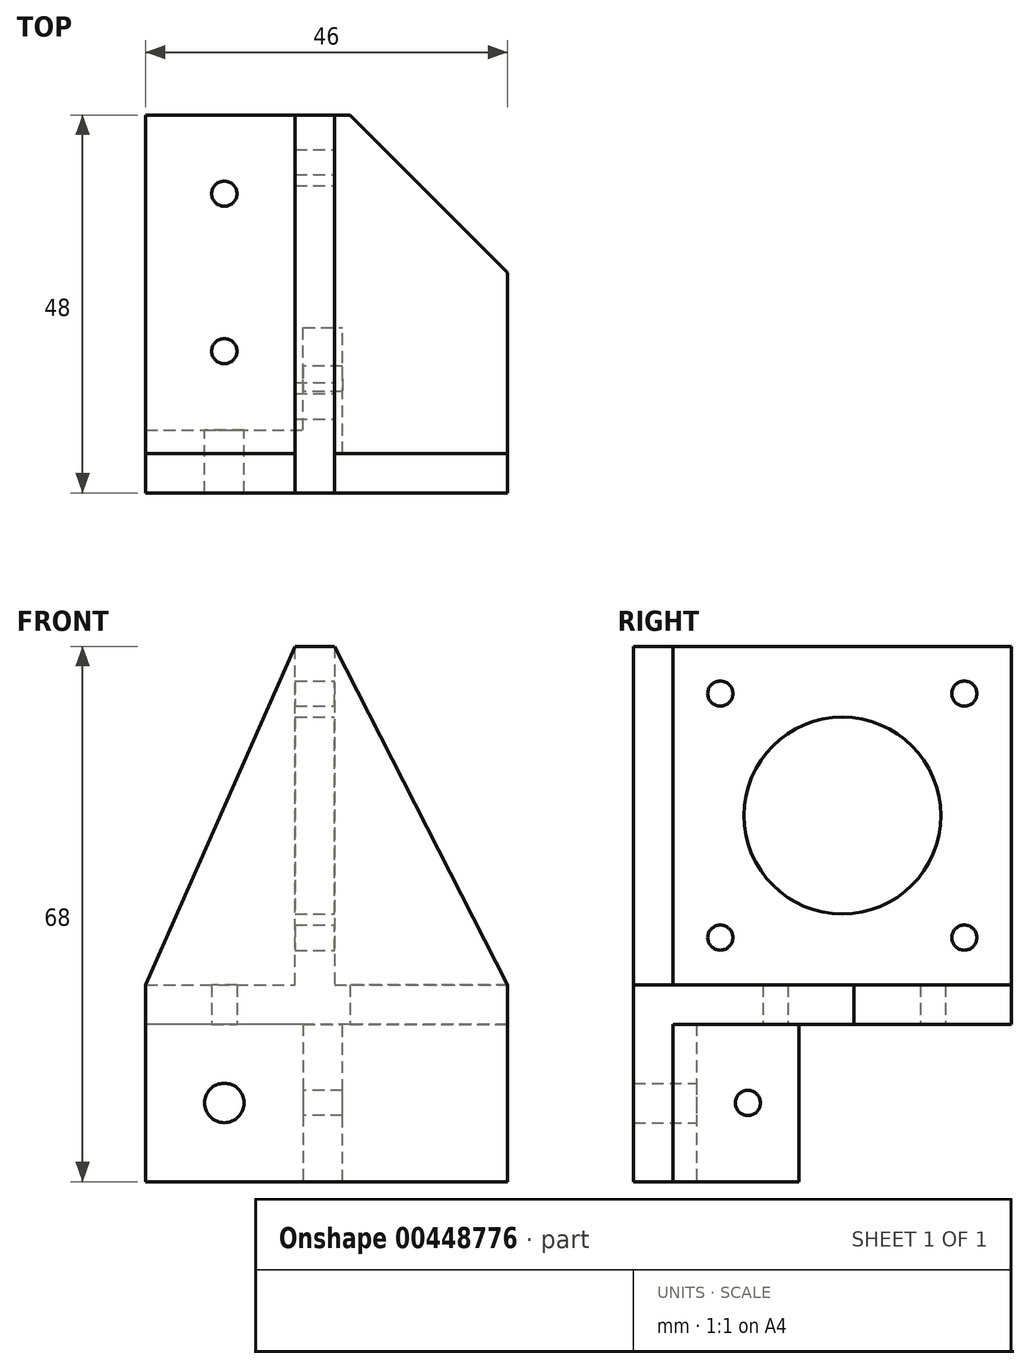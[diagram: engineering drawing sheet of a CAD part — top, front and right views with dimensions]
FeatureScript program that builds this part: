
annotation { "Feature Type Name" : "Feature", "Feature Type Description" : "" }
export const myFeature = defineFeature(function(context is Context, id is Id, definition is map)
    precondition{}
    {
        {
            var Q0;
            Q0=qCreatedBy(makeId("Front.planeOp"),FACE);
            var sketch = newSketch(context, id + "F0", { "sketchPlane" : qUnion([Q0])});
            skLineSegment(sketch, "E0.bottom", {"start": v(0, 20) * mm, "end": v(20, 20) * mm, "construction": true});
            skLineSegment(sketch, "E0.top", {"start": v(0, 0) * mm, "end": v(20, 0) * mm, "construction": true});
            skLineSegment(sketch, "E0.left", {"start": v(0, 20) * mm, "end": v(0, 0) * mm, "construction": true});
            skLineSegment(sketch, "E0.right", {"start": v(20, 20) * mm, "end": v(20, 0) * mm, "construction": true});
            skLineSegment(sketch, "E1", {"start": v(0, 20) * mm, "end": v(0, 25) * mm});
            skLineSegment(sketch, "E2", {"start": v(46, 25) * mm, "end": v(46, 20) * mm});
            skLineSegment(sketch, "E3", {"start": v(46, 20) * mm, "end": v(25, 20) * mm});
            skLineSegment(sketch, "E4", {"start": v(25, 20) * mm, "end": v(25, 0) * mm});
            skLineSegment(sketch, "E5", {"start": v(25, 0) * mm, "end": v(20, 0) * mm});
            skLineSegment(sketch, "E6", {"start": v(20, 20) * mm, "end": v(0, 20) * mm});
            skLineSegment(sketch, "E7", {"start": v(20, 20) * mm, "end": v(20, 0) * mm});
            skLineSegment(sketch, "E8", {"start": v(0, 25) * mm, "end": v(19, 25) * mm});
            skLineSegment(sketch, "E9", {"start": v(19, 25) * mm, "end": v(19, 68) * mm});
            skLineSegment(sketch, "E10", {"start": v(19, 68) * mm, "end": v(24, 68) * mm});
            skLineSegment(sketch, "E11", {"start": v(24, 68) * mm, "end": v(24, 25) * mm});
            skLineSegment(sketch, "E12", {"start": v(24, 25) * mm, "end": v(46, 25) * mm});
            skSolve(sketch);
        }
        {
            var Q0;
            Q0=makeQuery(id+"F0.imprint","IMPRINT",FACE,{"disambiguationData":[TD([[makeQuery(id+"F0.imprint","IMPRINT",EDGE,{"derivedFrom":sQuery(id+"F0.wireOp",EDGE,"E1")}),-1.0]])]});
            extrude(context, id + "F1", {"entities" : qUnion([Q0]), "depth" : 43 * mm});
        }
        {
            var Q0;
            Q0=makeQuery(id+"F1.opExtrude","CAP_FACE",FACE,{"disambiguationData":[OSD([sQuery(id+"F0.wireOp",EDGE,"E1"),sQuery(id+"F0.wireOp",EDGE,"E2"),sQuery(id+"F0.wireOp",EDGE,"E3"),sQuery(id+"F0.wireOp",EDGE,"E4"),sQuery(id+"F0.wireOp",EDGE,"E5"),sQuery(id+"F0.wireOp",EDGE,"E6"),sQuery(id+"F0.wireOp",EDGE,"E7"),sQuery(id+"F0.wireOp",EDGE,"E8"),sQuery(id+"F0.wireOp",EDGE,"E9"),sQuery(id+"F0.wireOp",EDGE,"E10"),sQuery(id+"F0.wireOp",EDGE,"E11"),sQuery(id+"F0.wireOp",EDGE,"E12")])],"isStart":false});
            var sketch = newSketch(context, id + "F2", { "sketchPlane" : qUnion([Q0])});
            skLineSegment(sketch, "E13.bottom", {"start": v(0, 20) * mm, "end": v(20, 20) * mm});
            skLineSegment(sketch, "E13.top", {"start": v(0, 0) * mm, "end": v(20, 0) * mm});
            skLineSegment(sketch, "E13.left", {"start": v(0, 20) * mm, "end": v(0, 0) * mm});
            skLineSegment(sketch, "E13.right", {"start": v(20, 20) * mm, "end": v(20, 0) * mm});
            skSolve(sketch);
        }
        {
            var Q0;
            Q0=qSketchRegion(id+"F2",true);
            extrude(context, id + "F3", {"entities" : qUnion([Q0]), "operationType" : NewBodyOperationType.ADD, "oppositeDirection" : true, "depth" : 3 * mm});
        }
        {
            var Q0;
            Q0=makeQuery(id+"F1.opExtrude","SWEPT_FACE",FACE,{"disambiguationData":[OSD([sQuery(id+"F0.wireOp",EDGE,"E4")])]});
            var sketch = newSketch(context, id + "F4", { "sketchPlane" : qUnion([Q0])});
            skLineSegment(sketch, "E14.bottom", {"start": v(0, 0) * mm, "end": v(-27, 0) * mm});
            skLineSegment(sketch, "E14.top", {"start": v(0, 20) * mm, "end": v(-27, 20) * mm});
            skLineSegment(sketch, "E14.left", {"start": v(0, 0) * mm, "end": v(0, 20) * mm});
            skLineSegment(sketch, "E14.right", {"start": v(-27, 0) * mm, "end": v(-27, 20) * mm});
            skSolve(sketch);
        }
        {
            var Q0;
            Q0=makeQuery(id+"F4.imprint","IMPRINT",FACE,{"disambiguationData":[TD([[makeQuery(id+"F4.imprint","IMPRINT",EDGE,{"derivedFrom":sQuery(id+"F4.wireOp",EDGE,"E14.bottom")}),1.0]])]});
            var Q1;
            Q1=makeQuery(id+"F1.opExtrude","SWEPT_FACE",FACE,{"disambiguationData":[OSD([sQuery(id+"F0.wireOp",EDGE,"E7")])]});
            extrude(context, id + "F5", {"entities" : qUnion([Q0]), "operationType" : NewBodyOperationType.REMOVE, "endBound" : BoundingType.UP_TO_SURFACE, "oppositeDirection" : true, "endBoundEntityFace" : qUnion([Q1]), "depth" : 25 * mm});
        }
        {
            var Q0;
            Q0=makeQuery(id+"F1.opExtrude","SWEPT_FACE",FACE,{"disambiguationData":[OSD([sQuery(id+"F0.wireOp",EDGE,"E11")])]});
            var sketch = newSketch(context, id + "F6", { "sketchPlane" : qUnion([Q0])});
            skLineSegment(sketch, "E15", {"start": v(-43, 68) * mm, "end": v(0, 25) * mm, "construction": true});
            skLineSegment(sketch, "E16", {"start": v(0, 68) * mm, "end": v(-43, 25) * mm, "construction": true});
            skPoint(sketch, "E17", {"position": v(-37, 62) * mm});
            skPoint(sketch, "E18", {"position": v(-6, 62) * mm});
            skPoint(sketch, "E19", {"position": v(-6, 31) * mm});
            skPoint(sketch, "E20", {"position": v(-37, 31) * mm});
            skSolve(sketch);
        }
        {
            var Q0;
            Q0=makeQuery(id+"F1.opExtrude","SWEPT_FACE",FACE,{"disambiguationData":[OSD([sQuery(id+"F0.wireOp",EDGE,"E11")])]});
            var sketch = newSketch(context, id + "F7", { "sketchPlane" : qUnion([Q0])});
            skCircle(sketch, "E21", {"center": v(-21.5, 46.5) * mm, "radius": 12.5 * mm});
            skPoint(sketch, "E21.centerSnap0", {"position": v(-43, 46.5) * mm});
            skPoint(sketch, "E21.centerSnap1", {"position": v(-21.5, 68) * mm});
            skSolve(sketch);
        }
        {
            var Q0;
            Q0=makeQuery(id+"F7.imprint","IMPRINT",FACE,{"disambiguationData":[TD([[makeQuery(id+"F7.imprint","IMPRINT",EDGE,{"derivedFrom":sQuery(id+"F7.wireOp",EDGE,"E21")}),1.0]])]});
            var Q1;
            Q1=makeQuery(id+"F1.opExtrude","SWEPT_FACE",FACE,{"disambiguationData":[OSD([sQuery(id+"F0.wireOp",EDGE,"E9")])]});
            extrude(context, id + "F8", {"entities" : qUnion([Q0]), "operationType" : NewBodyOperationType.REMOVE, "endBound" : BoundingType.UP_TO_SURFACE, "oppositeDirection" : true, "endBoundEntityFace" : qUnion([Q1]), "depth" : 25 * mm});
        }
        {
            var Q0;
            Q0=makeQuery(id+"F5.boolean.opBoolean","MERGE",FACE,{"derivedFrom":[makeQuery(id+"F1.opExtrude","SWEPT_FACE",FACE,{"disambiguationData":[OSD([sQuery(id+"F0.wireOp",EDGE,"E3")])]}),makeQuery(id+"F1.opExtrude","SWEPT_FACE",FACE,{"disambiguationData":[OSD([sQuery(id+"F0.wireOp",EDGE,"E6")])]}),makeQuery(id+"F5.opExtrude","SWEPT_FACE",FACE,{"disambiguationData":[OSD([sQuery(id+"F4.wireOp",EDGE,"E14.top")])]})]});
            var sketch = newSketch(context, id + "F9", { "sketchPlane" : qUnion([Q0])});
            skPoint(sketch, "E22", {"position": v(10, 30) * mm});
            skPoint(sketch, "E22.positionSnap0", {"position": v(10, 40) * mm});
            skPoint(sketch, "E23", {"position": v(10, 10) * mm});
            skSolve(sketch);
        }
        {
            var Q0;
            Q0=makeQuery(id+"F1.opExtrude","SWEPT_FACE",FACE,{"disambiguationData":[OSD([sQuery(id+"F0.wireOp",EDGE,"E7")])]});
            var sketch = newSketch(context, id + "F10", { "sketchPlane" : qUnion([Q0])});
            skPoint(sketch, "E24", {"position": v(33.5, 10) * mm});
            skPoint(sketch, "E24.positionSnap0", {"position": v(33.5, 0) * mm});
            skPoint(sketch, "E24.positionSnap1", {"position": v(27, 10) * mm});
            skSolve(sketch);
        }
        {
            var Q0;
            Q0=sQuery(id+"F6.wireOp",VERTEX,"E17");
            var Q1;
            Q1=sQuery(id+"F6.wireOp",VERTEX,"E18");
            var Q2;
            Q2=sQuery(id+"F6.wireOp",VERTEX,"E20");
            var Q3;
            Q3=sQuery(id+"F6.wireOp",VERTEX,"E19");
            var Q4;
            Q4=sQuery(id+"F9.wireOp",VERTEX,"E23");
            var Q5;
            Q5=sQuery(id+"F9.wireOp",VERTEX,"E22");
            var Q6;
            Q6=sQuery(id+"F10.wireOp",VERTEX,"E24");
            var Q7;
            Q7=makeQuery(id+"F1.opExtrude","SWEPT_BODY",BODY,{"disambiguationData":[OSD([sQuery(id+"F0.wireOp",EDGE,"E1"),sQuery(id+"F0.wireOp",EDGE,"E2"),sQuery(id+"F0.wireOp",EDGE,"E3"),sQuery(id+"F0.wireOp",EDGE,"E4"),sQuery(id+"F0.wireOp",EDGE,"E5"),sQuery(id+"F0.wireOp",EDGE,"E6"),sQuery(id+"F0.wireOp",EDGE,"E7"),sQuery(id+"F0.wireOp",EDGE,"E8"),sQuery(id+"F0.wireOp",EDGE,"E9"),sQuery(id+"F0.wireOp",EDGE,"E10"),sQuery(id+"F0.wireOp",EDGE,"E11"),sQuery(id+"F0.wireOp",EDGE,"E12")])]});
            hole(context, id + "F11", {"style" : HoleStyle.SIMPLE, "endStyle" : HoleEndStyle.THROUGH, "standardTappedOrClearance" : lookupTablePath({ "standard" : "ISO", "size" : "3.2", "type" : "Drilled" }), "standardBlindInLast" : lookupTablePath({ "standard" : "ISO", "size" : "3.2", "type" : "Drilled" }), "holeDiameter" : 3.2 * mm, "locations" : qUnion([Q0, Q1, Q2, Q3, Q4, Q5, Q6]), "scope" : qUnion([Q7]), "isTappedThrough" : true});
        }
        {
            var Q0;
            Q0=makeQuery(id+"F3.boolean.opBoolean","MERGE",FACE,{"derivedFrom":[makeQuery(id+"F1.opExtrude","CAP_FACE",FACE,{"disambiguationData":[OSD([sQuery(id+"F0.wireOp",EDGE,"E1"),sQuery(id+"F0.wireOp",EDGE,"E2"),sQuery(id+"F0.wireOp",EDGE,"E3"),sQuery(id+"F0.wireOp",EDGE,"E4"),sQuery(id+"F0.wireOp",EDGE,"E5"),sQuery(id+"F0.wireOp",EDGE,"E6"),sQuery(id+"F0.wireOp",EDGE,"E7"),sQuery(id+"F0.wireOp",EDGE,"E8"),sQuery(id+"F0.wireOp",EDGE,"E9"),sQuery(id+"F0.wireOp",EDGE,"E10"),sQuery(id+"F0.wireOp",EDGE,"E11"),sQuery(id+"F0.wireOp",EDGE,"E12")])],"isStart":false}),makeQuery(id+"F3.opExtrude","CAP_FACE",FACE,{"disambiguationData":[OSD([sQuery(id+"F2.wireOp",EDGE,"E13.bottom"),sQuery(id+"F2.wireOp",EDGE,"E13.top"),sQuery(id+"F2.wireOp",EDGE,"E13.left"),sQuery(id+"F2.wireOp",EDGE,"E13.right")])],"isStart":true})]});
            var sketch = newSketch(context, id + "F12", { "sketchPlane" : qUnion([Q0])});
            skLineSegment(sketch, "E25", {"start": v(0, 25) * mm, "end": v(19, 68) * mm});
            skLineSegment(sketch, "E26", {"start": v(19, 68) * mm, "end": v(24, 68) * mm});
            skLineSegment(sketch, "E27", {"start": v(24, 68) * mm, "end": v(46, 25) * mm});
            skLineSegment(sketch, "E28", {"start": v(46, 25) * mm, "end": v(46, 20) * mm});
            skLineSegment(sketch, "E29", {"start": v(0, 0) * mm, "end": v(0, 25) * mm});
            skLineSegment(sketch, "E30", {"start": v(0, 0) * mm, "end": v(46, 0) * mm});
            skLineSegment(sketch, "E31", {"start": v(46, 0) * mm, "end": v(46, 20) * mm});
            skSolve(sketch);
        }
        {
            var Q0;
            Q0=makeQuery(id+"F12.imprint","IMPRINT",FACE,{"disambiguationData":[TD([[makeQuery(id+"F12.imprint","IMPRINT",EDGE,{"derivedFrom":sQuery(id+"F12.wireOp",EDGE,"E25")}),-1.0]])]});
            var Q1;
            Q1=makeQuery(id+"F12.imprint","IMPRINT",FACE,{"disambiguationData":[TD([[makeQuery(id+"F12.imprint","IMPRINT",EDGE,{"derivedFrom":sQuery(id+"F12.wireOp",EDGE,"E26")}),-1.0]])]});
            var Q2;
            Q2=makeQuery(id+"F12.imprint","IMPRINT",FACE,{"disambiguationData":[TD([[makeQuery(id+"F12.imprint","IMPRINT",EDGE,{"derivedFrom":sQuery(id+"F12.wireOp",EDGE,"E27")}),-1.0]])]});
            var Q3;
            {var subQ2=sQuery(id+"F12.wireOp",EDGE,"E31");Q3=makeQuery(id+"F12.imprint","IMPRINT",FACE,{"disambiguationData":[TD([[makeQuery(id+"F12.imprint","IMPRINT",EDGE,{"derivedFrom":subQ2}),1.0]])]});}
            extrude(context, id + "F13", {"entities" : qUnion([Q0, Q1, Q2, Q3]), "operationType" : NewBodyOperationType.ADD, "depth" : 5 * mm});
        }
        {
            var Q0;
            Q0=makeQuery(id+"F1.opExtrude","CAP_EDGE",EDGE,{"disambiguationData":[OSD([sQuery(id+"F0.wireOp",EDGE,"E2")])],"isStart":true});
            chamfer(context, id + "F14", {"entities" : qUnion([Q0]), "width" : 20 * mm, "tangentPropagation" : true});
        }
        {
            var Q0;
            Q0=makeQuery(id+"F3.opExtrude","CAP_FACE",FACE,{"disambiguationData":[OSD([sQuery(id+"F2.wireOp",EDGE,"E13.bottom"),sQuery(id+"F2.wireOp",EDGE,"E13.top"),sQuery(id+"F2.wireOp",EDGE,"E13.left"),sQuery(id+"F2.wireOp",EDGE,"E13.right")])],"isStart":false});
            var sketch = newSketch(context, id + "F15", { "sketchPlane" : qUnion([Q0])});
            skPoint(sketch, "E32", {"position": v(-10, 0) * mm});
            skPoint(sketch, "E33", {"position": v(0, 10) * mm});
            skCircle(sketch, "E34", {"center": v(-10, 10) * mm, "radius": 2.5 * mm});
            skSolve(sketch);
        }
        {
            var Q0;
            Q0=makeQuery(id+"F15.imprint","IMPRINT",FACE,{"disambiguationData":[TD([[makeQuery(id+"F15.imprint","IMPRINT",EDGE,{"derivedFrom":sQuery(id+"F15.wireOp",EDGE,"E34")}),1.0]])]});
            var Q1;
            Q1=makeQuery(id+"F13.opExtrude","CAP_FACE",FACE,{"disambiguationData":[OSD([sQuery(id+"F12.wireOp",EDGE,"E25"),sQuery(id+"F12.wireOp",EDGE,"E26"),sQuery(id+"F12.wireOp",EDGE,"E27"),sQuery(id+"F12.wireOp",EDGE,"E28"),sQuery(id+"F12.wireOp",EDGE,"E29"),sQuery(id+"F12.wireOp",EDGE,"E30"),sQuery(id+"F12.wireOp",EDGE,"E31")])],"isStart":false});
            extrude(context, id + "F16", {"entities" : qUnion([Q0]), "operationType" : NewBodyOperationType.REMOVE, "endBound" : BoundingType.UP_TO_SURFACE, "oppositeDirection" : true, "endBoundEntityFace" : qUnion([Q1]), "depth" : 25 * mm});
        }
    });
